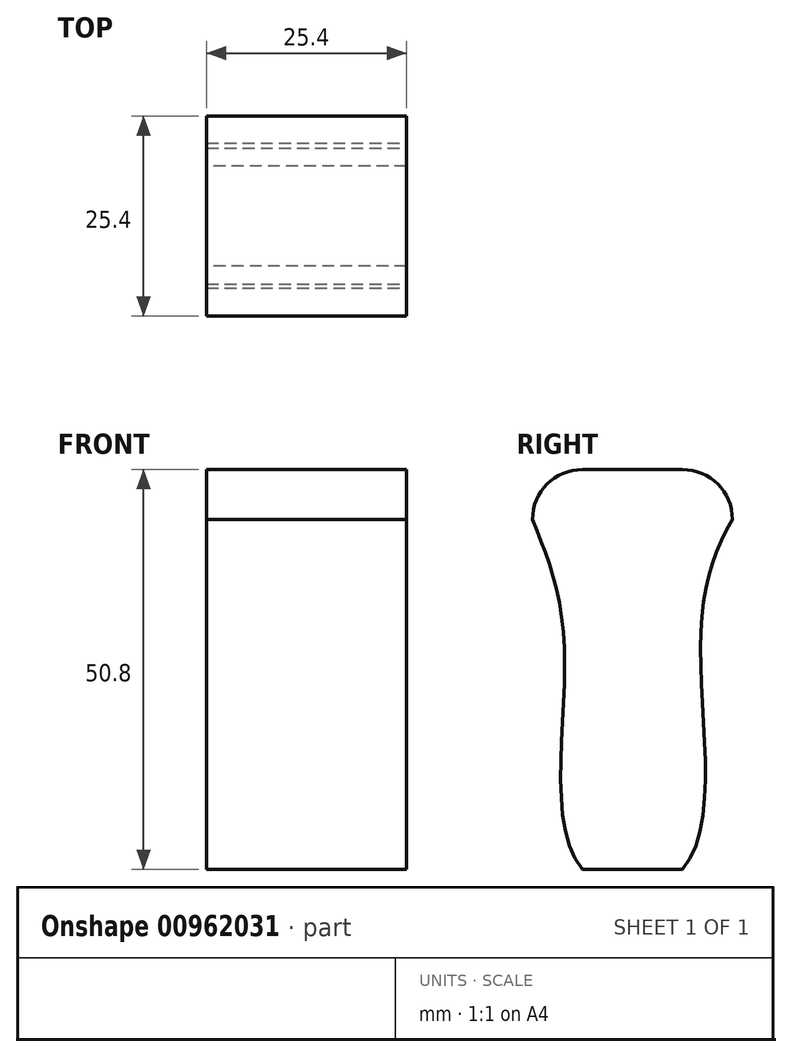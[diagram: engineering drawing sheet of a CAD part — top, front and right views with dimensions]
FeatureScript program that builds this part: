
annotation { "Feature Type Name" : "Feature", "Feature Type Description" : "" }
export const myFeature = defineFeature(function(context is Context, id is Id, definition is map)
    precondition{}
    {
        {
            var Q0;
            Q0=qCreatedBy(makeId("Right.planeOp"),FACE);
            var sketch = newSketch(context, id + "F0", { "sketchPlane" : qUnion([Q0])});
            skLineSegment(sketch, "E0.bottom", {"start": v(6.35, 0) * mm, "end": v(19.05, 0) * mm});
            skLineSegment(sketch, "E0.top", {"start": v(6.35, -50.8) * mm, "end": v(19.05, -50.8) * mm});
            skLineSegment(sketch, "E0.left", {"start": v(0, -6.35) * mm, "end": v(0, -44.45) * mm});
            skLineSegment(sketch, "E0.right", {"start": v(25.4, -6.35) * mm, "end": v(25.4, -44.45) * mm});
            skPoint(sketch, "E1.visualSharp", {"position": v(0, 0) * mm});
            skArc(sketch, "E1.filletArc", {"start": v(6.35, 0) * mm, "mid": v(1.86, -1.86) * mm, "end": v(0, -6.35) * mm});
            skPoint(sketch, "E2.visualSharp", {"position": v(25.4, 0) * mm});
            skArc(sketch, "E2.filletArc", {"start": v(25.4, -6.35) * mm, "mid": v(23.54, -1.86) * mm, "end": v(19.05, 0) * mm});
            skPoint(sketch, "E3.visualSharp", {"position": v(25.4, -50.8) * mm});
            skArc(sketch, "E3.filletArc", {"start": v(19.05, -50.8) * mm, "mid": v(23.54, -48.94) * mm, "end": v(25.4, -44.45) * mm});
            skPoint(sketch, "E4.visualSharp", {"position": v(0, -50.8) * mm});
            skArc(sketch, "E4.filletArc", {"start": v(0, -44.45) * mm, "mid": v(1.86, -48.94) * mm, "end": v(6.35, -50.8) * mm});
            skFitSpline(sketch, "E5", {"points": [v(25.4, -6.35) * mm, v(21.34, -22.86) * mm, v(19.05, -50.8) * mm, v(6.35, -50.8) * mm, v(4.06, -22.86) * mm, v(0, -6.35) * mm], "startDerivative": vector(-42.54, -71.7) * mm, "endDerivative": vector(-29.56, 74.6) * mm});
            skSolve(sketch);
        }
        {
            var Q0;
            Q0=makeQuery(id+"F0.imprint","IMPRINT",FACE,{"disambiguationData":[TD([[makeQuery(id+"F0.imprint","IMPRINT",EDGE,{"derivedFrom":sQuery(id+"F0.wireOp",EDGE,"E0.bottom")}),-1.0]])]});
            extrude(context, id + "F1", {"entities" : qUnion([Q0]), "depth" : 25.4 * mm, "offsetDistance" : 25.4 * mm});
        }
    });
